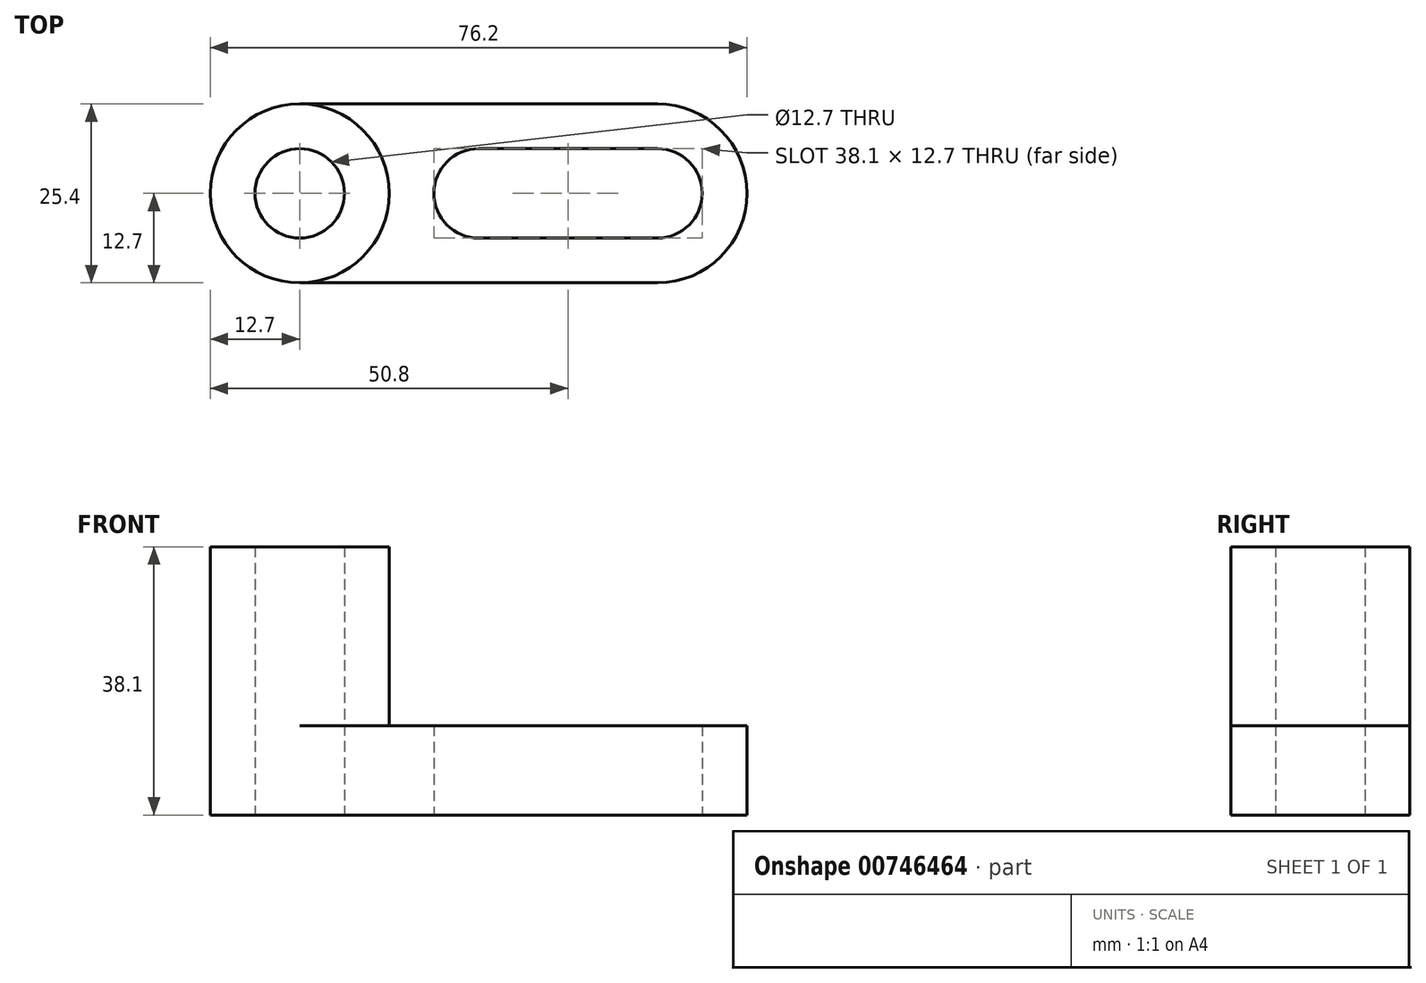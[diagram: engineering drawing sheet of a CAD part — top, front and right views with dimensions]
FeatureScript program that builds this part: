
annotation { "Feature Type Name" : "Feature", "Feature Type Description" : "" }
export const myFeature = defineFeature(function(context is Context, id is Id, definition is map)
    precondition{}
    {
        {
            var Q0;
            Q0=qCreatedBy(makeId("Top.planeOp"),FACE);
            var sketch = newSketch(context, id + "F0", { "sketchPlane" : qUnion([Q0])});
            skLineSegment(sketch, "E0.bottom", {"start": v(0, 0) * mm, "end": v(50.8, 0) * mm});
            skLineSegment(sketch, "E0.top", {"start": v(0, 25.4) * mm, "end": v(50.8, 25.4) * mm});
            skLineSegment(sketch, "E0.left", {"start": v(0, 0) * mm, "end": v(0, 25.4) * mm});
            skLineSegment(sketch, "E0.right", {"start": v(50.8, 0) * mm, "end": v(50.8, 25.4) * mm});
            skArc(sketch, "E1", {"start": v(0, 25.4) * mm, "mid": v(-12.7, 12.7) * mm, "end": v(0, 0) * mm});
            skArc(sketch, "E2", {"start": v(50.8, 0) * mm, "mid": v(63.5, 12.7) * mm, "end": v(50.8, 25.4) * mm});
            skCircle(sketch, "E3", {"center": v(0, 12.7) * mm, "radius": 6.35 * mm});
            skLineSegment(sketch, "E4.bottom", {"start": v(50.8, 6.35) * mm, "end": v(25.4, 6.35) * mm});
            skLineSegment(sketch, "E4.top", {"start": v(50.8, 19.05) * mm, "end": v(25.4, 19.05) * mm});
            skLineSegment(sketch, "E4.left", {"start": v(50.8, 6.35) * mm, "end": v(50.8, 19.05) * mm});
            skLineSegment(sketch, "E4.right", {"start": v(25.4, 6.35) * mm, "end": v(25.4, 19.05) * mm});
            skArc(sketch, "E5", {"start": v(25.4, 19.05) * mm, "mid": v(19.05, 12.7) * mm, "end": v(25.4, 6.35) * mm});
            skArc(sketch, "E6", {"start": v(50.8, 6.35) * mm, "mid": v(57.15, 12.7) * mm, "end": v(50.8, 19.05) * mm});
            skArc(sketch, "E7", {"start": v(0, 0) * mm, "mid": v(12.7, 12.7) * mm, "end": v(0, 25.4) * mm});
            skSolve(sketch);
        }
        {
            var Q0;
            {var subQ1=sQuery(id+"F0.wireOp",EDGE,"E1");Q0=makeQuery(id+"F0.imprint","IMPRINT",FACE,{"disambiguationData":[TD([[makeQuery(id+"F0.imprint","IMPRINT",EDGE,{"derivedFrom":subQ1}),1.0]])]});}
            var Q1;
            {var subQ0=sQuery(id+"F0.wireOp",EDGE,"E7");Q1=makeQuery(id+"F0.imprint","IMPRINT",FACE,{"disambiguationData":[TD([[makeQuery(id+"F0.imprint","IMPRINT",EDGE,{"derivedFrom":subQ0}),1.0]])]});}
            extrude(context, id + "F1", {"entities" : qUnion([Q0, Q1]), "depth" : 38.1 * mm, "offsetDistance" : 25.4 * mm});
        }
        {
            var Q0;
            {var subQ6=sQuery(id+"F0.wireOp",EDGE,"E0.bottom");Q0=makeQuery(id+"F0.imprint","IMPRINT",FACE,{"disambiguationData":[TD([[makeQuery(id+"F0.imprint","IMPRINT",EDGE,{"derivedFrom":subQ6}),1.0]])]});}
            var Q1;
            {var subQ0=sQuery(id+"F0.wireOp",EDGE,"E2");Q1=makeQuery(id+"F0.imprint","IMPRINT",FACE,{"disambiguationData":[TD([[makeQuery(id+"F0.imprint","IMPRINT",EDGE,{"derivedFrom":subQ0}),1.0]])]});}
            extrude(context, id + "F2", {"entities" : qUnion([Q0, Q1]), "operationType" : NewBodyOperationType.ADD, "depth" : 12.7 * mm, "offsetDistance" : 25.4 * mm});
        }
    });
